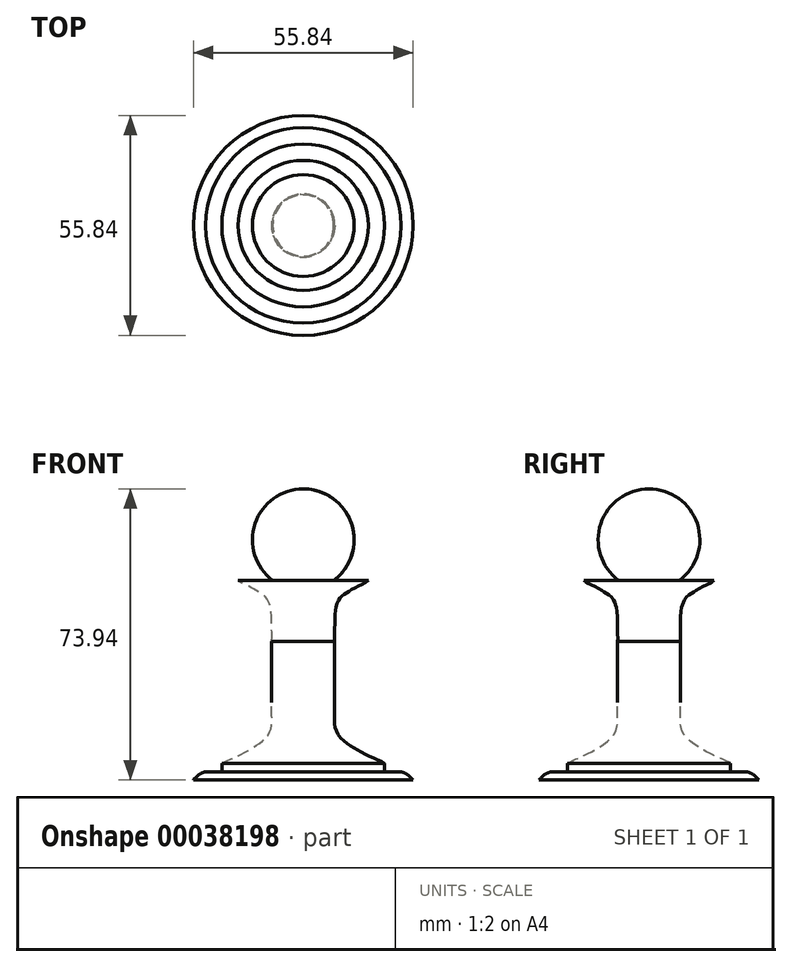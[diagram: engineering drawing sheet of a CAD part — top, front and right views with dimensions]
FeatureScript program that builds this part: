
annotation { "Feature Type Name" : "Feature", "Feature Type Description" : "" }
export const myFeature = defineFeature(function(context is Context, id is Id, definition is map)
    precondition{}
    {
        {
            var Q0;
            Q0=qCreatedBy(makeId("Front.planeOp"),FACE);
            var sketch = newSketch(context, id + "F0", { "sketchPlane" : qUnion([Q0])});
            skArc(sketch, "E0", {"start": v(7.76, 14.72) * mm, "mid": v(12.26, 29.15) * mm, "end": v(0, 37.99) * mm});
            skLineSegment(sketch, "E1", {"start": v(7.76, 14.72) * mm, "end": v(16.54, 14.72) * mm});
            skLineSegment(sketch, "E2", {"start": v(8, -0.79) * mm, "end": v(8, -16.3) * mm});
            skLineSegment(sketch, "E3", {"start": v(20.68, -33.88) * mm, "end": v(24.82, -33.88) * mm});
            skLineSegment(sketch, "E4", {"start": v(0, -35.95) * mm, "end": v(27.92, -35.95) * mm});
            skFitSpline(sketch, "E5", {"points": [v(16.54, 14.72) * mm, v(13.26, 12.94) * mm, v(11, 11.56) * mm, v(9.5, 10.44) * mm, v(8.38, 8.19) * mm, v(8.02, 4.79) * mm, v(8, 2.2) * mm, v(8, -0.79) * mm], "startDerivative": vector(-12.96, -12.3) * mm, "endDerivative": vector(2.3, -19.32) * mm});
            skFitSpline(sketch, "E6", {"points": [v(20.68, -31.81) * mm, v(20.68, -33.88) * mm], "startDerivative": vector(0, -2.07) * mm, "endDerivative": vector(0, -2.07) * mm});
            skFitSpline(sketch, "E7", {"points": [v(24.82, -33.88) * mm, v(26.31, -34.5) * mm, v(27.92, -35.95) * mm], "startDerivative": vector(3, -0.7) * mm, "endDerivative": vector(3.2, -3.32) * mm});
            skFitSpline(sketch, "E8", {"points": [v(8, -16.3) * mm, v(8, -17.84) * mm, v(8, -19.58) * mm, v(8, -21.7) * mm, v(8.77, -24.26) * mm, v(11.31, -26.81) * mm, v(14.03, -28.5) * mm, v(17.73, -30.35) * mm, v(20.68, -31.81) * mm], "startDerivative": vector(-0.07, -15.7) * mm, "endDerivative": vector(16.72, -14.56) * mm});
            skPoint(sketch, "E9.start.orphan", {"position": v(0, -16.3) * mm});
            skPoint(sketch, "E10.end.orphan", {"position": v(0, -33.88) * mm});
            skLineSegment(sketch, "E11", {"start": v(0, 37.99) * mm, "end": v(0, -35.95) * mm});
            skSolve(sketch);
        }
        {
            var Q0;
            Q0 = qSketchRegion(id + "F0", true);
            var Q1;
            Q1=sQuery(id+"F0.wireOp",EDGE,"E11");
            revolve(context, id + "F1", {"entities" : qUnion([Q0]), "axis" : qUnion([Q1]), "revolveType" : RevolveType.FULL});
        }
    });
